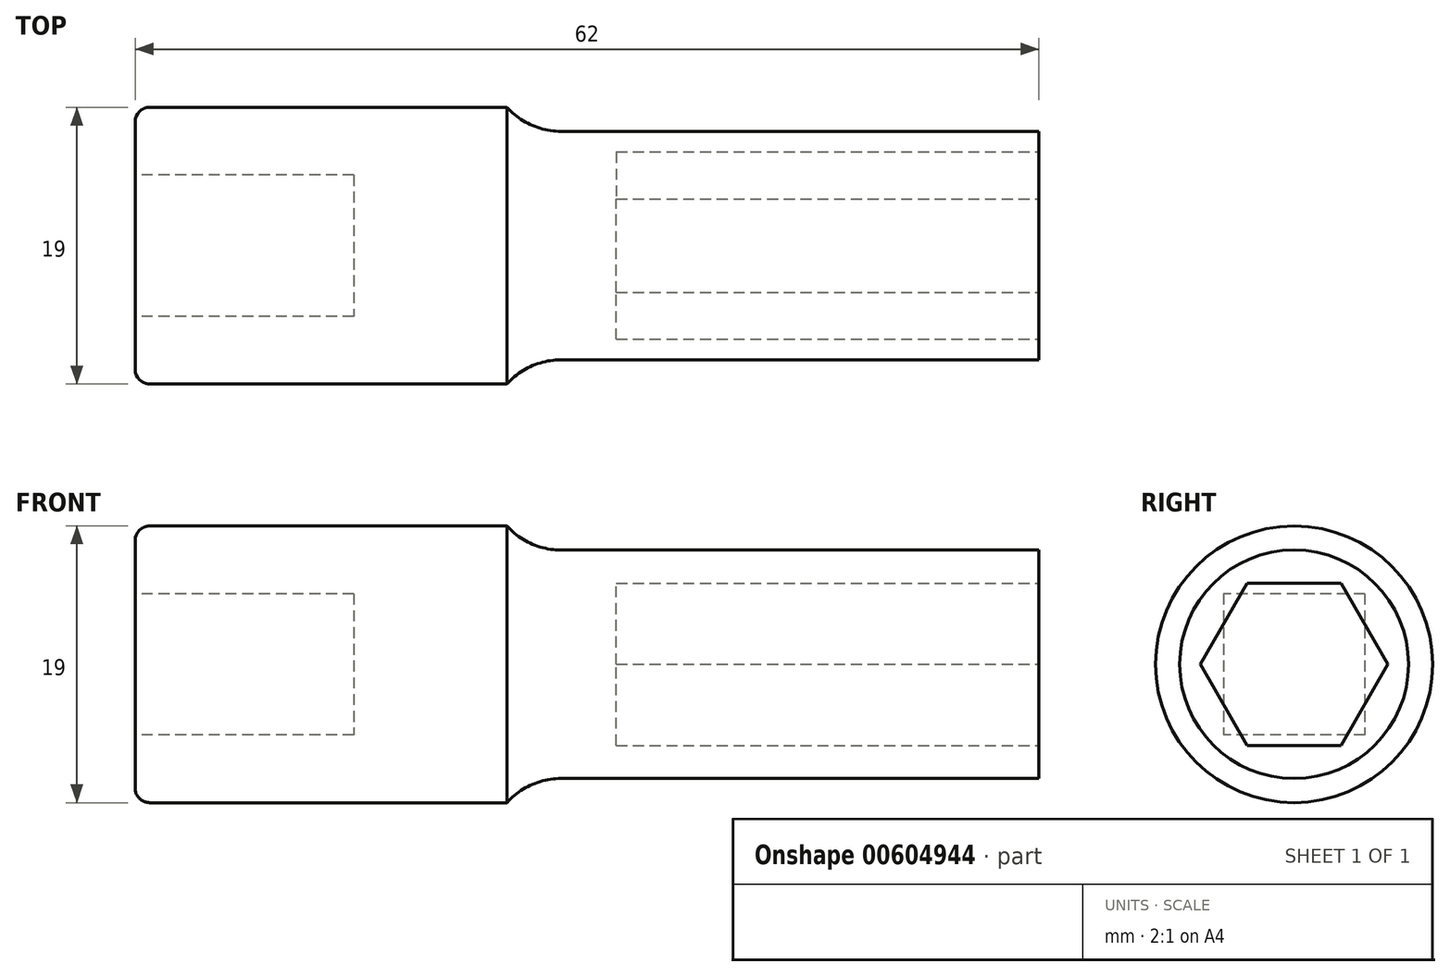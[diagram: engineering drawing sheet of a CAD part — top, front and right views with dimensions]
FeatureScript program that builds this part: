
annotation { "Feature Type Name" : "Feature", "Feature Type Description" : "" }
export const myFeature = defineFeature(function(context is Context, id is Id, definition is map)
    precondition{}
    {
        {
            var Q0;
            Q0=qCreatedBy(makeId("Right.planeOp"),FACE);
            var sketch = newSketch(context, id + "F0", { "sketchPlane" : qUnion([Q0])});
            skCircle(sketch, "E0", {"center": v(0, 0) * mm, "radius": 9.5 * mm});
            skSolve(sketch);
        }
        {
            var Q0;
            Q0=makeQuery(id+"F0.imprint","IMPRINT",FACE,{"disambiguationData":[TD([[makeQuery(id+"F0.imprint","IMPRINT",EDGE,{"derivedFrom":sQuery(id+"F0.wireOp",EDGE,"E0")}),1.0]])]});
            extrude(context, id + "F1", {"entities" : qUnion([Q0]), "endBound" : BoundingType.SYMMETRIC, "depth" : 62 * mm, "offsetDistance" : 25 * mm});
        }
        {
            var Q0;
            Q0=makeQuery(id+"F1.opExtrude","CAP_FACE",FACE,{"disambiguationData":[OSD([sQuery(id+"F0.wireOp",EDGE,"E0")])],"isStart":false});
            var sketch = newSketch(context, id + "F2", { "sketchPlane" : qUnion([Q0])});
            skCircle(sketch, "E1", {"center": v(0, 0) * mm, "radius": 7.84 * mm});
            skSolve(sketch);
        }
        {
            var Q0;
            Q0=makeQuery(id+"F2.imprint","IMPRINT",FACE,{"disambiguationData":[TD([[makeQuery(id+"F2.imprint","IMPRINT",EDGE,{"derivedFrom":sQuery(id+"F2.wireOp",EDGE,"E1")}),-1.0]])]});
            extrude(context, id + "F3", {"entities" : qUnion([Q0]), "operationType" : NewBodyOperationType.REMOVE, "oppositeDirection" : true, "depth" : 36.5 * mm, "offsetDistance" : 25 * mm});
        }
        {
            var Q0;
            Q0=makeQuery(id+"F3.boolean.opBoolean","COPY",EDGE,{"derivedFrom":makeQuery(id+"F3.opExtrude","CAP_EDGE",EDGE,{"disambiguationData":[OSD([sQuery(id+"F2.wireOp",EDGE,"E1")])],"isStart":false})});
            fillet(context, id + "F4", {"entities" : qUnion([Q0]), "radius" : 5 * mm, "tangentPropagation" : true, "allowEdgeOverflow" : false});
        }
        {
            var Q0;
            Q0=makeQuery(id+"F3.boolean.opBoolean","COPY",EDGE,{"derivedFrom":makeQuery(id+"F3.opExtrude","CAP_EDGE",EDGE,{"disambiguationData":[OSD([sQuery(id+"F2.wireOp",EDGE,"E1")])],"isStart":true})});
            var Q1;
            Q1=makeQuery(id+"F1.opExtrude","CAP_EDGE",EDGE,{"disambiguationData":[OSD([sQuery(id+"F0.wireOp",EDGE,"E0")])],"isStart":true});
            fillet(context, id + "F5", {"entities" : qUnion([Q0, Q1]), "radius" : 1 * mm, "tangentPropagation" : true, "allowEdgeOverflow" : false});
        }
        {
            var Q0;
            Q0=makeQuery(id+"F1.opExtrude","CAP_FACE",FACE,{"disambiguationData":[OSD([sQuery(id+"F0.wireOp",EDGE,"E0")])],"isStart":false});
            var sketch = newSketch(context, id + "F6", { "sketchPlane" : qUnion([Q0])});
            skCircle(sketch, "E2.cCircle", {"center": v(0, 0) * mm, "radius": 5.57 * mm, "construction": true});
            skLineSegment(sketch, "E2.0", {"start": v(-3.21, 5.57) * mm, "end": v(3.21, 5.57) * mm});
            skLineSegment(sketch, "E2.1", {"start": v(3.21, 5.57) * mm, "end": v(6.43, 0) * mm});
            skLineSegment(sketch, "E2.2", {"start": v(6.43, 0) * mm, "end": v(3.21, -5.56) * mm});
            skLineSegment(sketch, "E2.3", {"start": v(3.21, -5.56) * mm, "end": v(-3.21, -5.57) * mm});
            skLineSegment(sketch, "E2.4", {"start": v(-3.21, -5.57) * mm, "end": v(-6.43, 0) * mm});
            skLineSegment(sketch, "E2.5", {"start": v(-6.43, 0) * mm, "end": v(-3.21, 5.57) * mm});
            skPoint(sketch, "E2.0.midPoint", {"position": v(0, 5.57) * mm});
            skSolve(sketch);
        }
        {
            var Q0;
            Q0=makeQuery(id+"F6.imprint","IMPRINT",FACE,{"disambiguationData":[TD([[makeQuery(id+"F6.imprint","IMPRINT",EDGE,{"derivedFrom":sQuery(id+"F6.wireOp",EDGE,"E2.0")}),-1.0]])]});
            extrude(context, id + "F7", {"entities" : qUnion([Q0]), "operationType" : NewBodyOperationType.REMOVE, "oppositeDirection" : true, "depth" : 29 * mm, "offsetDistance" : 25 * mm});
        }
        {
            var Q0;
            Q0=makeQuery(id+"F1.opExtrude","CAP_FACE",FACE,{"disambiguationData":[OSD([sQuery(id+"F0.wireOp",EDGE,"E0")])],"isStart":true});
            var sketch = newSketch(context, id + "F8", { "sketchPlane" : qUnion([Q0])});
            skLineSegment(sketch, "E3.bottom", {"start": v(-4.85, 4.85) * mm, "end": v(4.85, 4.85) * mm});
            skLineSegment(sketch, "E3.top", {"start": v(-4.85, -4.85) * mm, "end": v(4.85, -4.85) * mm});
            skLineSegment(sketch, "E3.left", {"start": v(-4.85, 4.85) * mm, "end": v(-4.85, -4.85) * mm});
            skLineSegment(sketch, "E3.right", {"start": v(4.85, 4.85) * mm, "end": v(4.85, -4.85) * mm});
            skSolve(sketch);
        }
        {
            var Q0;
            Q0=makeQuery(id+"F8.imprint","IMPRINT",FACE,{"disambiguationData":[TD([[makeQuery(id+"F8.imprint","IMPRINT",EDGE,{"derivedFrom":sQuery(id+"F8.wireOp",EDGE,"E3.bottom")}),-1.0]])]});
            extrude(context, id + "F9", {"entities" : qUnion([Q0]), "operationType" : NewBodyOperationType.REMOVE, "oppositeDirection" : true, "depth" : 15 * mm, "offsetDistance" : 25 * mm});
        }
    });
